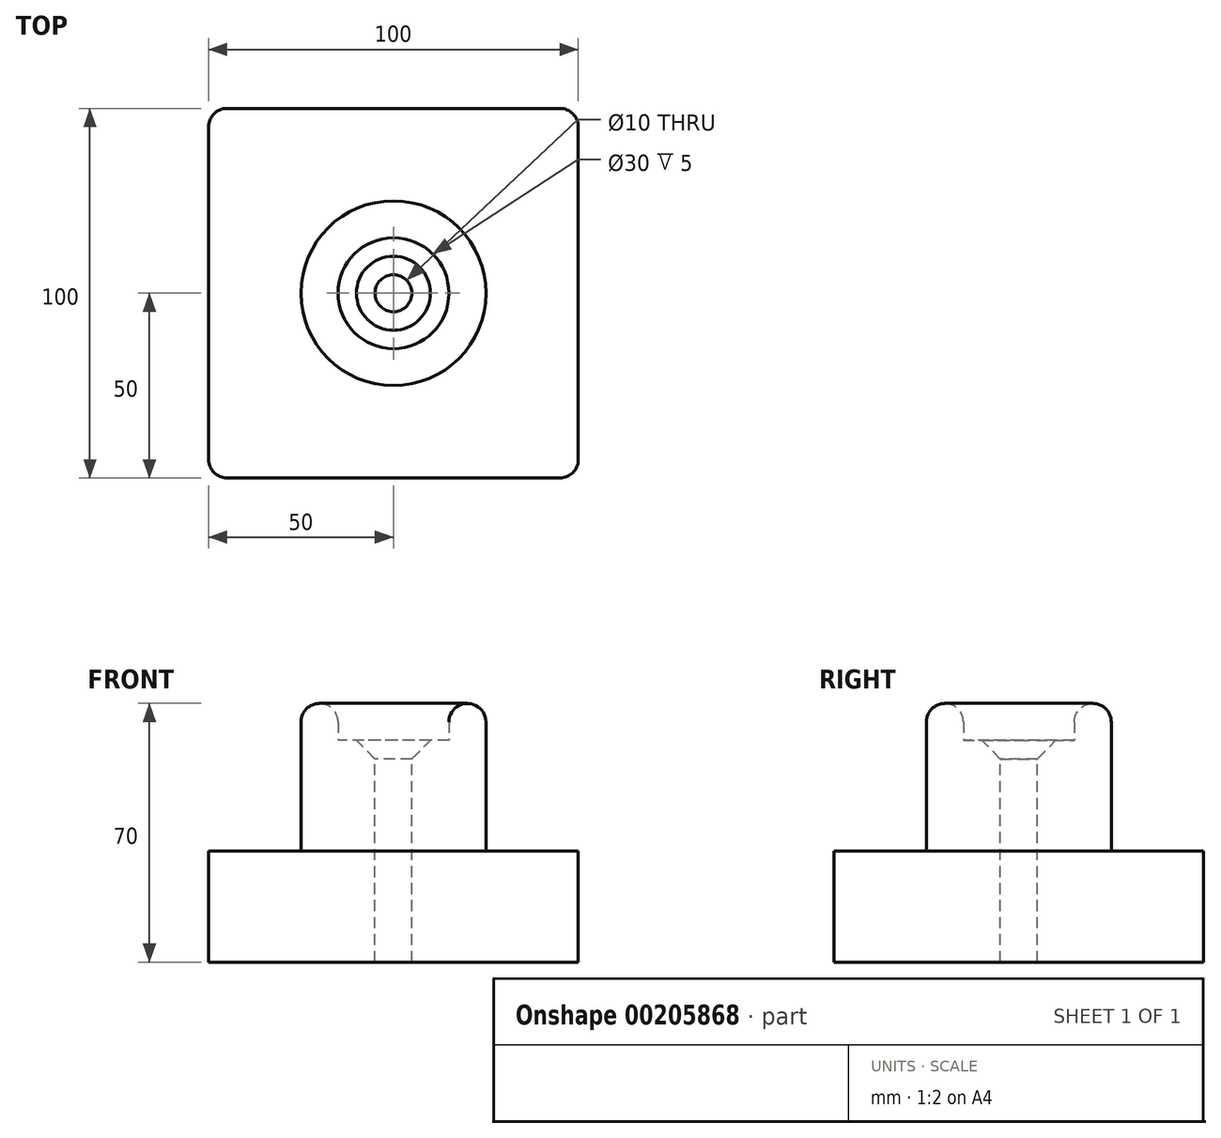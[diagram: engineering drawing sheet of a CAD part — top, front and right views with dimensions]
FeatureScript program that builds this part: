
annotation { "Feature Type Name" : "Feature", "Feature Type Description" : "" }
export const myFeature = defineFeature(function(context is Context, id is Id, definition is map)
    precondition{}
    {
        {
            var Q0;
            Q0=qCreatedBy(makeId("Front.planeOp"),FACE);
            var sketch = newSketch(context, id + "F0", { "sketchPlane" : qUnion([Q0])});
            skLineSegment(sketch, "E0.bottom", {"start": v(25, 15) * mm, "end": v(-25, 15) * mm});
            skLineSegment(sketch, "E0.top", {"start": v(25, 45) * mm, "end": v(-25, 45) * mm});
            skLineSegment(sketch, "E0.left", {"start": v(25, 15) * mm, "end": v(25, 45) * mm});
            skLineSegment(sketch, "E0.right", {"start": v(-25, 15) * mm, "end": v(-25, 45) * mm});
            skPoint(sketch, "E0.middle", {"position": v(0, 30) * mm});
            skLineSegment(sketch, "E1.bottom", {"start": v(50, 15) * mm, "end": v(-50, 15) * mm});
            skLineSegment(sketch, "E1.top", {"start": v(50, -15) * mm, "end": v(-50, -15) * mm});
            skLineSegment(sketch, "E1.left", {"start": v(50, 15) * mm, "end": v(50, -15) * mm});
            skLineSegment(sketch, "E1.right", {"start": v(-50, 15) * mm, "end": v(-50, -15) * mm});
            skPoint(sketch, "E1.middle", {"position": v(0, 0) * mm});
            skLineSegment(sketch, "E2", {"start": v(0, 45) * mm, "end": v(0, -15) * mm});
            skSolve(sketch);
        }
        {
            var Q0;
            Q0=makeQuery(id+"F0.imprint","IMPRINT",FACE,{"disambiguationData":[TD([[makeQuery(id+"F0.imprint","IMPRINT",EDGE,{"derivedFrom":sQuery(id+"F0.wireOp",EDGE,"E1.top")}),-1.0]])]});
            extrude(context, id + "F1", {"entities" : qUnion([Q0]), "endBound" : BoundingType.SYMMETRIC, "depth" : 100 * mm});
        }
        {
            var Q0;
            {var subQ0=sQuery(id+"F0.wireOp",EDGE,"E0.right");Q0=makeQuery(id+"F0.imprint","IMPRINT",FACE,{"disambiguationData":[TD([[makeQuery(id+"F0.imprint","IMPRINT",EDGE,{"derivedFrom":subQ0}),-1.0]])]});}
            var Q1;
            Q1=sQuery(id+"F0.wireOp",EDGE,"E2");
            revolve(context, id + "F2", {"operationType" : NewBodyOperationType.ADD, "entities" : qUnion([Q0]), "axis" : qUnion([Q1]), "revolveType" : RevolveType.FULL});
        }
        {
            var Q0;
            Q0=makeQuery(id+"F2.opRevolve","SWEPT_FACE",FACE,{"disambiguationData":[OSD([sQuery(id+"F0.wireOp",EDGE,"E0.top")])]});
            var sketch = newSketch(context, id + "F3", { "sketchPlane" : qUnion([Q0])});
            skCircle(sketch, "E3", {"center": v(0, 0) * mm, "radius": 15 * mm});
            skSolve(sketch);
        }
        {
            var Q0;
            Q0=sQuery(id+"F3.wireOp",VERTEX,"E3.center");
            var Q1;
            Q1=makeQuery(id+"F1.opExtrude","SWEPT_BODY",BODY,{"disambiguationData":[OSD([sQuery(id+"F0.wireOp",EDGE,"E1.bottom"),sQuery(id+"F0.wireOp",EDGE,"E1.top"),sQuery(id+"F0.wireOp",EDGE,"E1.left"),sQuery(id+"F0.wireOp",EDGE,"E1.right")])]});
            hole(context, id + "F4", {"style" : HoleStyle.C_SINK, "endStyle" : HoleEndStyle.THROUGH, "holeDiameter" : 10 * mm, "cSinkDiameter" : 20 * mm, "cSinkAngle" : 90 * degree, "startFromSketch" : true, "locations" : qUnion([Q0]), "scope" : qUnion([Q1]), "isTappedThrough" : true});
        }
        {
            var Q0;
            Q0=makeQuery(id+"F1.opExtrude","CAP_EDGE",EDGE,{"disambiguationData":[OSD([sQuery(id+"F0.wireOp",EDGE,"E1.right")])],"isStart":true});
            var Q1;
            Q1=makeQuery(id+"F1.opExtrude","CAP_EDGE",EDGE,{"disambiguationData":[OSD([sQuery(id+"F0.wireOp",EDGE,"E1.left")])],"isStart":true});
            var Q2;
            Q2=makeQuery(id+"F1.opExtrude","CAP_EDGE",EDGE,{"disambiguationData":[OSD([sQuery(id+"F0.wireOp",EDGE,"E1.left")])],"isStart":false});
            var Q3;
            Q3=makeQuery(id+"F1.opExtrude","CAP_EDGE",EDGE,{"disambiguationData":[OSD([sQuery(id+"F0.wireOp",EDGE,"E1.right")])],"isStart":false});
            fillet(context, id + "F5", {"entities" : qUnion([Q0, Q1, Q2, Q3]), "radius" : 5 * mm, "tangentPropagation" : true, "allowEdgeOverflow" : false});
        }
        {
            var Q0;
            Q0=makeQuery(id+"F3.imprint","IMPRINT",FACE,{"disambiguationData":[TD([[makeQuery(id+"F3.imprint","IMPRINT",EDGE,{"derivedFrom":sQuery(id+"F3.wireOp",EDGE,"E3")}),-1.0]])]});
            extrude(context, id + "F6", {"entities" : qUnion([Q0]), "operationType" : NewBodyOperationType.ADD, "depth" : 10 * mm});
        }
        {
            var Q0;
            Q0=makeQuery(id+"F6.opExtrude","CAP_EDGE",EDGE,{"disambiguationData":[OSD([sQuery(id+"F0.wireOp",EDGE,"E0.top"),sQuery(id+"F0.wireOp",EDGE,"E0.right")])],"isStart":false});
            var Q1;
            Q1=makeQuery(id+"F6.opExtrude","CAP_EDGE",EDGE,{"disambiguationData":[OSD([sQuery(id+"F3.wireOp",EDGE,"E3")])],"isStart":false});
            fillet(context, id + "F7", {"entities" : qUnion([Q0, Q1]), "radius" : 5 * mm, "tangentPropagation" : true, "allowEdgeOverflow" : false});
        }
    });
